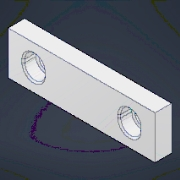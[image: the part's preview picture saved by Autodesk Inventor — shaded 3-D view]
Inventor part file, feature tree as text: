
AUTODESK INVENTOR PART (.ipt)
format: ipt  version: 2024.3 (Build 283343000, 343)  size: 248,320 bytes
history: native  units: mm
features: extrude x5, chamfer x3, sketch x2, fillet x1, projected_geometry x1
ambient origin geometry x8: Origin, YZ Plane, XZ Plane, XY Plane, X Axis, Y Axis, Z Axis, Center Point
bodies: Solid1 (feature_tree)
feature tree (12):
  sketch  "Sketch1"  dims[d0=44.5mm d1=151.0mm]
  extrude  "Extrusion1"  Depth=151.0mm
  extrude  "Extrusion2"  TaperAngle=0.0deg  [1 undecoded]
  extrude  "Extrusion3"  Depth=2.0mm TaperAngle=45.0deg
  chamfer  "Chamfer3"  Distance=14.0mm
  chamfer  "Chamfer4"  Distance=20.7mm
  chamfer  "Chamfer5"  Distance=98.42mm
  sketch  "Sketch2"  dims[d4=18.0mm d5=0.0mm d19=1.0mm d20=2.0mm d21=45.0deg d26=14.0mm d27=20.7mm d28=98.42mm d29=21.0mm d30=1.55mm d31=0.0mm d32=0.0mm d33=12.78mm d34=0.0mm d35=1.5mm d36=2.0mm d37=45.0deg d38=0.5mm d39=2.0mm d40=45.0deg d54=95.0mm d57=45.0deg d59=70.0mm d60=45.0deg d61=85.0mm d62=100.0mm d63=35.0mm d64=0.0mm d65=6.0mm d66=0.0mm d68=2.0mm d69=10.0mm d50=0.5mm d51=0.872665mm d52=0.5mm d53=0.872665mm]
  extrude  "Extrusion6"  Depth=21.0mm
  extrude  "Extrusion7"  Depth=10.0mm
  fillet  "Fillet1"  [1 undecoded]
  projected_geometry  "Projected Loop1"
note: 2 required parameter values undecoded (feature->parameter linkage not recoverable at this tier; creation-order binding heuristic only, values carry confidence <= 0.55)
